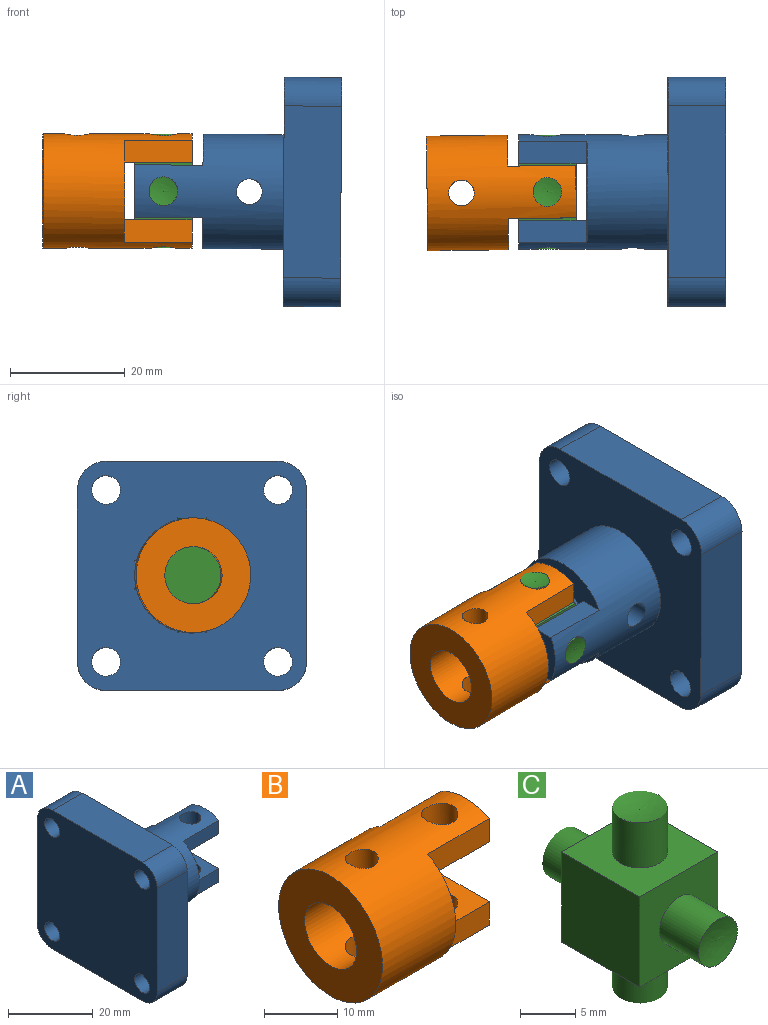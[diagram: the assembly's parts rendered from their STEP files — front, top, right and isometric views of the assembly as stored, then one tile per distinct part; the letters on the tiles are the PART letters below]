
ASSEMBLY  parts=3 mates=2
PART A: 31 faces, bbox 36x40x40 mm
  f0: plane 9.16x5mm, normal (1,0,0), area 42.5mm2, adj f2,f4,f5,f15
  f1: cylinder r=5mm len=14.11mm, axis (1,0,0), area 410.7mm2, adj f7,f9,f10,f12,f26
  f2: plane 11.89x3.89mm, normal (0,1,0), area 46.2mm2, adj f0,f5,f7,f15
  f3: cylinder r=2.5mm len=5mm, axis (0,0,-1), area 76.1mm2, adj f5,f15
  f4: plane 11.89x3.89mm, normal (0,-1,0), area 46.2mm2, adj f0,f5,f12,f15
  f5: cylinder r=10mm len=26mm, axis (1,0,0), area 1041.4mm2, adj f0,f2,f3,f4,f6,f7,f8,f9
  f6: plane 9.16x5mm, normal (1,0,0), area 42.5mm2, adj f5,f8,f13,f14
  f7: plane 17.78x10mm, normal (1,0,0), area 75.3mm2, adj f1,f2,f5,f8,f14,f15
  f8: plane 11.89x3.89mm, normal (0,1,0), area 46.2mm2, adj f5,f6,f7,f14
  f9: cylinder r=2.25mm len=5.54mm, axis (0,0,-1), area 72.6mm2, adj f1,f5
  f10: cylinder r=2.25mm len=5.54mm, axis (0,0,-1), area 72.6mm2, adj f1,f5
  f11: cylinder r=2.5mm len=5mm, axis (0,0,-1), area 76.1mm2, adj f5,f14
  f12: plane 17.78x10mm, normal (1,0,0), area 75.3mm2, adj f1,f4,f5,f13,f14,f15
  f13: plane 11.89x3.89mm, normal (0,-1,0), area 46.2mm2, adj f5,f6,f12,f14
  f14: plane 11.89x9.16mm, normal (0,0,-1), area 89.2mm2, adj f6,f7,f8,f11,f12,f13
  f15: plane 11.89x9.16mm, normal (0,0,1), area 89.2mm2, adj f0,f2,f3,f4,f7,f12
  f16: plane 40x40mm, normal (1,0,0), area 1185.8mm2, adj f5,f18,f19,f20,f21,f22,f23,f24
  f17: plane 40x40mm, normal (-1,0,0), area 1500mm2, adj f18,f19,f20,f21,f22,f23,f24,f25
  f18: plane 30x10mm, normal (0,-1,0), area 300mm2, adj f16,f17,f29,f30
  f19: cylinder r=2.5mm len=10mm, axis (1,0,0), area 157.1mm2, adj f16,f17
  f20: cylinder r=2.5mm len=10mm, axis (1,0,0), area 157.1mm2, adj f16,f17
  f21: cylinder r=2.5mm len=10mm, axis (1,0,0), area 157.1mm2, adj f16,f17
  f22: cylinder r=2.5mm len=10mm, axis (1,0,0), area 157.1mm2, adj f16,f17
  f23: plane 30x10mm, normal (0,0,-1), area 300mm2, adj f16,f17,f28,f29
  f24: plane 30x10mm, normal (0,1,0), area 300mm2, adj f16,f17,f27,f28
  f25: plane 30x10mm, normal (0,0,1), area 300mm2, adj f16,f17,f27,f30
  f26: plane 10x10mm, normal (1,0,0), area 78.5mm2, adj f1
  f27: cylinder r=5mm len=10mm, axis (-1,0,0), area 78.5mm2, adj f16,f17,f24,f25
  f28: cylinder r=5mm len=10mm, axis (1,0,0), area 78.5mm2, adj f16,f17,f23,f24
  f29: cylinder r=5mm len=10mm, axis (-1,0,0), area 78.5mm2, adj f16,f17,f18,f23
  f30: cylinder r=5mm len=10mm, axis (1,0,0), area 78.5mm2, adj f16,f17,f18,f25
PART B: 17 faces, bbox 26x20x20 mm
  f0: plane 9.16x5mm, normal (1,0,0), area 42.5mm2, adj f2,f4,f5,f16
  f1: cylinder r=5mm len=14.11mm, axis (1,0,0), area 410.7mm2, adj f7,f8,f10,f11,f13
  f2: plane 11.89x3.89mm, normal (0,1,0), area 46.2mm2, adj f0,f5,f8,f16
  f3: cylinder r=2.5mm len=5mm, axis (0,0,-1), area 76.1mm2, adj f5,f16
  f4: plane 11.89x3.89mm, normal (0,-1,0), area 46.2mm2, adj f0,f5,f13,f16
  f5: cylinder r=10mm len=26mm, axis (1,0,0), area 1041.4mm2, adj f0,f2,f3,f4,f6,f7,f8,f9
  f6: plane 9.16x5mm, normal (1,0,0), area 42.5mm2, adj f5,f9,f14,f15
  f7: plane 20x20mm, normal (-1,0,0), area 235.6mm2, adj f1,f5
  f8: plane 17.78x10mm, normal (1,0,0), area 75.3mm2, adj f1,f2,f5,f9,f15,f16
  f9: plane 11.89x3.89mm, normal (0,1,0), area 46.2mm2, adj f5,f6,f8,f15
  f10: cylinder r=2.25mm len=5.54mm, axis (0,0,-1), area 72.6mm2, adj f1,f5
  f11: cylinder r=2.25mm len=5.54mm, axis (0,0,-1), area 72.6mm2, adj f1,f5
  f12: cylinder r=2.5mm len=5mm, axis (0,0,-1), area 76.1mm2, adj f5,f15
  f13: plane 17.78x10mm, normal (1,0,0), area 75.3mm2, adj f1,f4,f5,f14,f15,f16
  f14: plane 11.89x3.89mm, normal (0,-1,0), area 46.2mm2, adj f5,f6,f13,f15
  f15: plane 11.89x9.16mm, normal (0,0,-1), area 89.2mm2, adj f6,f8,f9,f12,f13,f14
  f16: plane 11.89x9.16mm, normal (0,0,1), area 89.2mm2, adj f0,f2,f3,f4,f8,f13
PART C: 14 faces, bbox 10x20x20 mm
  f0: revolved ~5x5mm, area 19.9mm2, adj f1
  f1: cylinder r=2.5mm len=5mm, axis (0,0,1), area 78.5mm2, adj f0,f4
  f2: cylinder r=2.5mm len=5mm, axis (0,-1,0), area 78.5mm2, adj f3,f8
  f3: revolved ~5x5mm, area 19.9mm2, adj f2
  f4: plane 10x10mm, normal (0,0,-1), area 80.4mm2, adj f1,f5,f7,f8,f9
  f5: plane 10x10mm, normal (1,0,0), area 100mm2, adj f4,f6,f8,f9
  f6: plane 10x10mm, normal (0,0,1), area 80.4mm2, adj f5,f7,f8,f9,f13
  f7: plane 10x10mm, normal (-1,0,0), area 100mm2, adj f4,f6,f8,f9
  f8: plane 10x10mm, normal (0,-1,0), area 80.4mm2, adj f2,f4,f5,f6,f7
  f9: plane 10x10mm, normal (0,1,0), area 80.4mm2, adj f4,f5,f6,f7,f11
  f10: revolved ~5x5mm, area 19.9mm2, adj f11
  f11: cylinder r=2.5mm len=5mm, axis (0,-1,0), area 78.5mm2, adj f9,f10
  f12: revolved ~5x5mm, area 19.9mm2, adj f13
  f13: cylinder r=2.5mm len=5mm, axis (0,0,1), area 78.5mm2, adj f6,f12
PLACE A rot(axis=(0,-0.71,-0.71),179.8deg) t=(0,0,0)mm
PLACE B rot(axis=(0,0,1),0.7deg) t=(0,0,0)mm
PLACE C at identity fixed
MATE revolute C.f2 <-> A.f3  axis (0,1,0) through (0,5,0)mm
MATE revolute C.f1 <-> B.f3  axis (0,0,1) through (0,0,5)mm
